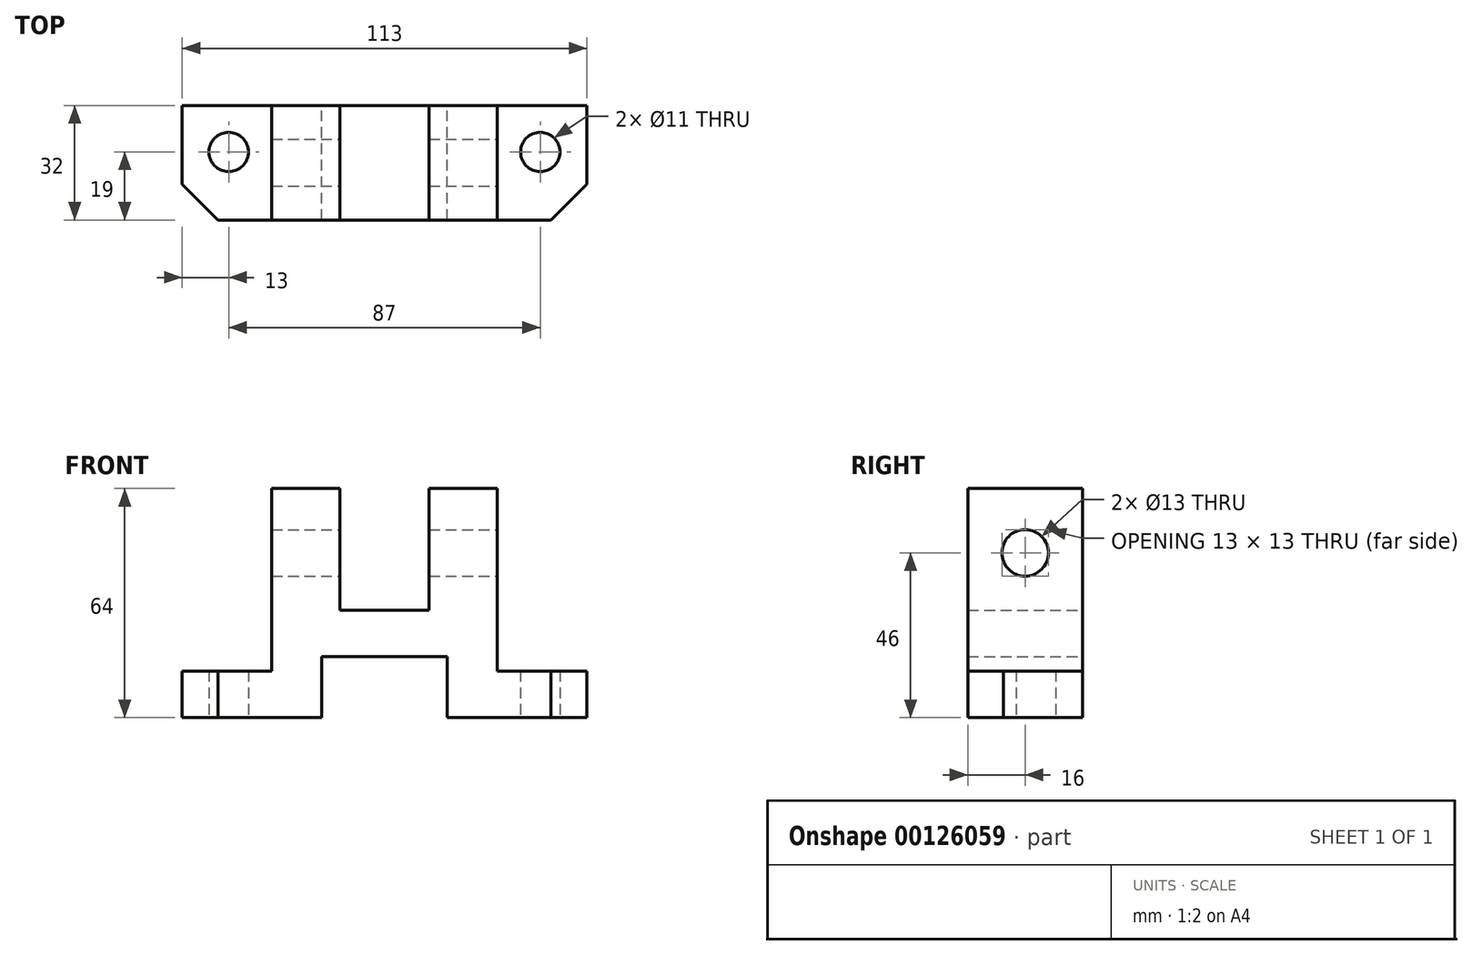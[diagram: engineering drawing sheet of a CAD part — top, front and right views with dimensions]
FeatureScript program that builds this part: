
annotation { "Feature Type Name" : "Feature", "Feature Type Description" : "" }
export const myFeature = defineFeature(function(context is Context, id is Id, definition is map)
    precondition{}
    {
        {
            var Q0;
            Q0=qCreatedBy(makeId("Front.planeOp"),FACE);
            var sketch = newSketch(context, id + "F0", { "sketchPlane" : qUnion([Q0])});
            skLineSegment(sketch, "E0", {"start": v(-56.5, 0) * mm, "end": v(-56.5, 13) * mm});
            skLineSegment(sketch, "E1", {"start": v(-56.5, 13) * mm, "end": v(-31.5, 13) * mm});
            skLineSegment(sketch, "E2", {"start": v(-31.5, 13) * mm, "end": v(-31.5, 64) * mm});
            skLineSegment(sketch, "E3", {"start": v(-31.5, 64) * mm, "end": v(-12.5, 64) * mm});
            skLineSegment(sketch, "E4", {"start": v(-12.5, 64) * mm, "end": v(-12.5, 30) * mm});
            skLineSegment(sketch, "E5", {"start": v(-12.5, 30) * mm, "end": v(12.5, 30) * mm});
            skLineSegment(sketch, "E6", {"start": v(12.5, 30) * mm, "end": v(12.5, 64) * mm});
            skLineSegment(sketch, "E7", {"start": v(12.5, 64) * mm, "end": v(31.5, 64) * mm});
            skLineSegment(sketch, "E8", {"start": v(31.5, 64) * mm, "end": v(31.5, 13) * mm});
            skLineSegment(sketch, "E9", {"start": v(31.5, 13) * mm, "end": v(56.5, 13) * mm});
            skLineSegment(sketch, "E10", {"start": v(56.5, 13) * mm, "end": v(56.5, 0) * mm});
            skLineSegment(sketch, "E11", {"start": v(-56.5, 0) * mm, "end": v(56.5, 0) * mm});
            skLineSegment(sketch, "E12", {"start": v(-17.5, 0) * mm, "end": v(-17.5, 17) * mm});
            skLineSegment(sketch, "E13", {"start": v(-17.5, 17) * mm, "end": v(17.5, 17) * mm});
            skLineSegment(sketch, "E14", {"start": v(17.5, 17) * mm, "end": v(17.5, 0) * mm});
            skLineSegment(sketch, "E15", {"start": v(-17.5, 0) * mm, "end": v(17.5, 0) * mm});
            skSolve(sketch);
        }
        {
            var Q0;
            {var subQ0=sQuery(id+"F0.wireOp",EDGE,"E0");Q0=makeQuery(id+"F0.imprint","IMPRINT",FACE,{"disambiguationData":[TD([[makeQuery(id+"F0.imprint","IMPRINT",EDGE,{"derivedFrom":subQ0}),-1.0]])]});}
            extrude(context, id + "F1", {"entities" : qUnion([Q0]), "endBound" : BoundingType.SYMMETRIC, "depth" : 32 * mm});
        }
        {
            var Q0;
            Q0=qCreatedBy(makeId("Right.planeOp"),FACE);
            var sketch = newSketch(context, id + "F2", { "sketchPlane" : qUnion([Q0])});
            skCircle(sketch, "E16", {"center": v(0, 46) * mm, "radius": 6.5 * mm});
            skSolve(sketch);
        }
        {
            var Q0;
            Q0 = qSketchRegion(id + "F2", true);
            extrude(context, id + "F3", {"entities" : qUnion([Q0]), "operationType" : NewBodyOperationType.REMOVE, "endBound" : BoundingType.SYMMETRIC, "oppositeDirection" : true, "depth" : (19 + 19 + 35) * mm});
        }
        {
            var Q0;
            Q0=qCreatedBy(makeId("Top.planeOp"),FACE);
            var sketch = newSketch(context, id + "F4", { "sketchPlane" : qUnion([Q0])});
            skCircle(sketch, "E17", {"center": v(-43.5, 3) * mm, "radius": 5.5 * mm});
            skCircle(sketch, "E18", {"center": v(43.5, 3) * mm, "radius": 5.5 * mm});
            skSolve(sketch);
        }
        {
            var Q0;
            Q0 = qSketchRegion(id + "F4", true);
            extrude(context, id + "F5", {"entities" : qUnion([Q0]), "operationType" : NewBodyOperationType.REMOVE, "depth" : 13 * mm});
        }
        {
            var Q0;
            Q0=makeQuery(id+"F1.opExtrude","CAP_EDGE",EDGE,{"disambiguationData":[OSD([sQuery(id+"F0.wireOp",EDGE,"E10")])],"isStart":false});
            var Q1;
            Q1=makeQuery(id+"F1.opExtrude","CAP_EDGE",EDGE,{"disambiguationData":[OSD([sQuery(id+"F0.wireOp",EDGE,"E0")])],"isStart":false});
            chamfer(context, id + "F6", {"entities" : qUnion([Q0, Q1]), "width" : 10 * mm, "tangentPropagation" : true});
        }
    });
